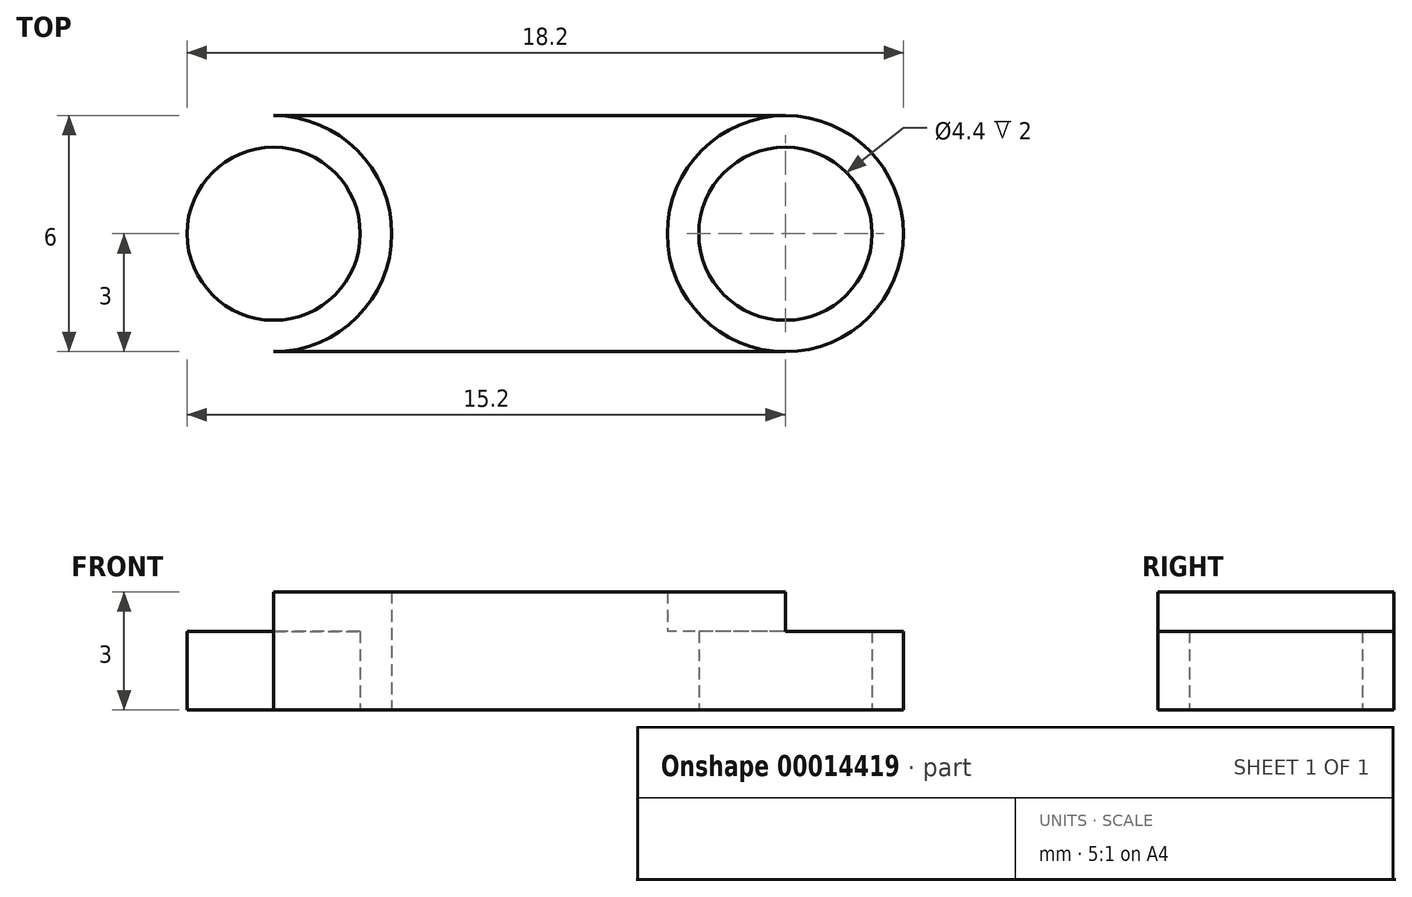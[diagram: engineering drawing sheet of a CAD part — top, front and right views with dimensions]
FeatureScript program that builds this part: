
annotation { "Feature Type Name" : "Feature", "Feature Type Description" : "" }
export const myFeature = defineFeature(function(context is Context, id is Id, definition is map)
    precondition{}
    {
        {
            var Q0;
            Q0=qCreatedBy(makeId("Top.planeOp"),FACE);
            var sketch = newSketch(context, id + "F0", { "sketchPlane" : qUnion([Q0])});
            skLineSegment(sketch, "E0", {"start": v(0, 0) * mm, "end": v(6.5, 0) * mm, "construction": true});
            skCircle(sketch, "E1", {"center": v(6.5, 0) * mm, "radius": 3 * mm});
            skLineSegment(sketch, "E2.MirrorCS", {"start": v(0, 0) * mm, "end": v(-6.5, 0) * mm});
            skCircle(sketch, "E3.MirrorC", {"center": v(-6.5, 0) * mm, "radius": 3 * mm});
            skCircle(sketch, "E4", {"center": v(6.5, 0) * mm, "radius": 2.2 * mm});
            skCircle(sketch, "E5.MirrorC", {"center": v(-6.5, 0) * mm, "radius": 2.2 * mm});
            skLineSegment(sketch, "E6", {"start": v(0, 0) * mm, "end": v(0, -3) * mm, "construction": true});
            skLineSegment(sketch, "E7", {"start": v(0, -3) * mm, "end": v(6.5, -3) * mm});
            skLineSegment(sketch, "E8", {"start": v(6.5, -3) * mm, "end": v(-6.5, -3) * mm});
            skLineSegment(sketch, "E9.MirrorCS", {"start": v(6.5, 3) * mm, "end": v(-6.5, 3) * mm});
            skSolve(sketch);
        }
        {
            var Q0;
            {var subQ0=sQuery(id+"F0.wireOp",EDGE,"E9.MirrorCS");Q0=makeQuery(id+"F0.imprint","IMPRINT",FACE,{"disambiguationData":[TD([[makeQuery(id+"F0.imprint","IMPRINT",EDGE,{"derivedFrom":subQ0}),1.0]])]});}
            extrude(context, id + "F1", {"entities" : qUnion([Q0]), "depth" : 3 * mm});
        }
        {
            var Q0;
            Q0=makeQuery(id+"F0.imprint","IMPRINT",FACE,{"disambiguationData":[TD([[makeQuery(id+"F0.imprint","IMPRINT",EDGE,{"derivedFrom":sQuery(id+"F0.wireOp",EDGE,"E5.MirrorC")}),1.0]])]});
            var Q1;
            Q1=makeQuery(id+"F0.imprint","IMPRINT",FACE,{"disambiguationData":[TD([[makeQuery(id+"F0.imprint","IMPRINT",EDGE,{"derivedFrom":sQuery(id+"F0.wireOp",EDGE,"E4")}),-1.0]])]});
            extrude(context, id + "F2", {"entities" : qUnion([Q0, Q1]), "operationType" : NewBodyOperationType.ADD, "depth" : 2 * mm});
        }
    });
